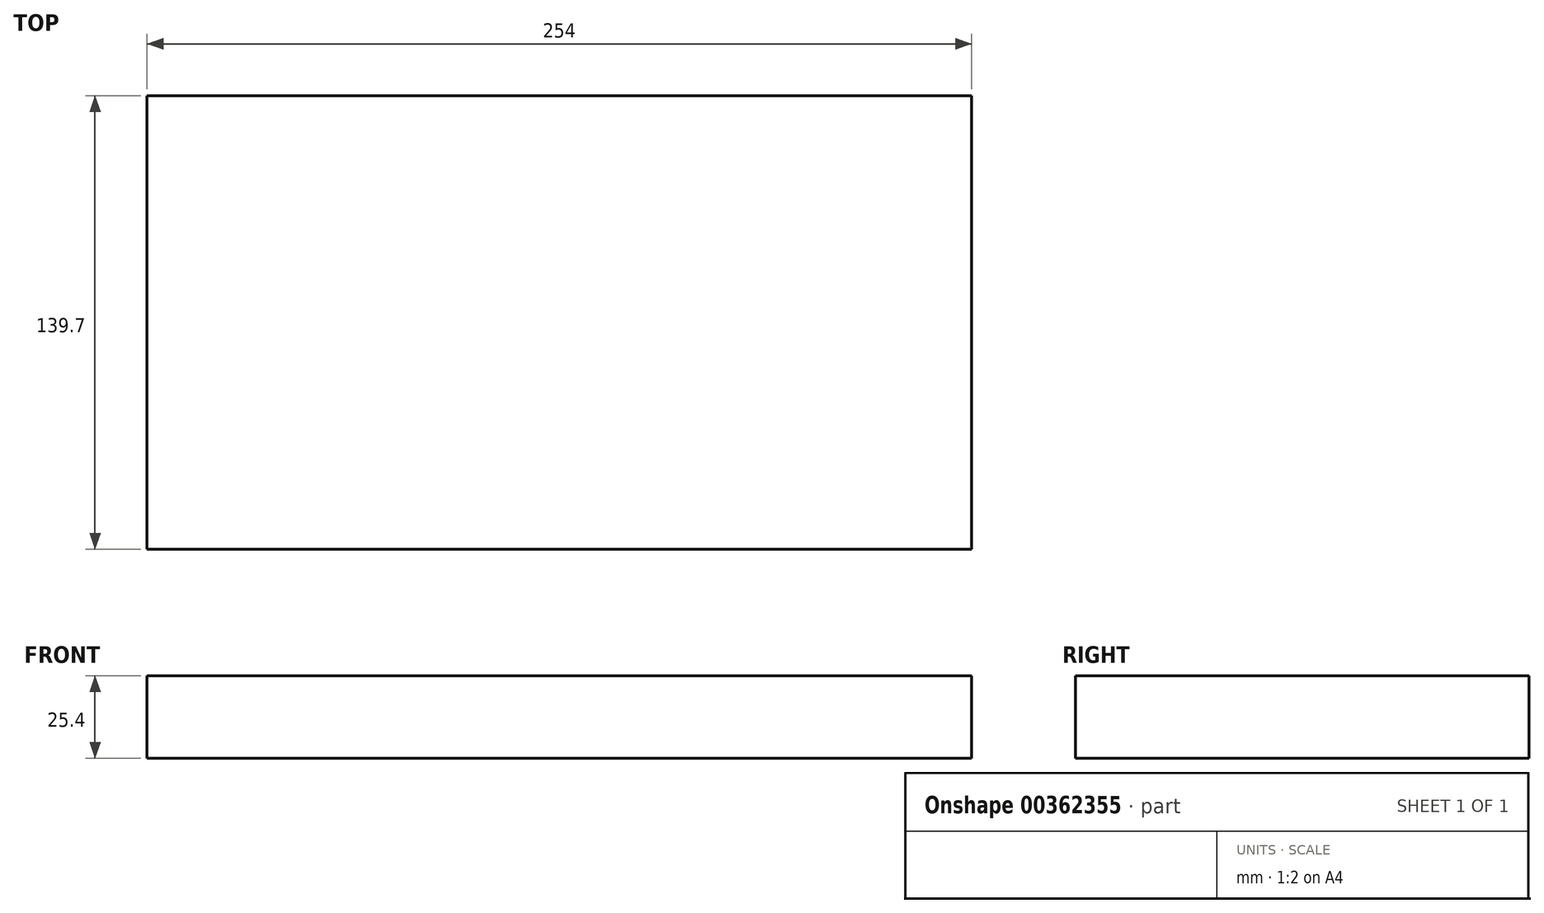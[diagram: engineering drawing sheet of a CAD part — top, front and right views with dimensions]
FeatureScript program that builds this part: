
annotation { "Feature Type Name" : "Feature", "Feature Type Description" : "" }
export const myFeature = defineFeature(function(context is Context, id is Id, definition is map)
    precondition{}
    {
        {
            var Q0;
            Q0=qCreatedBy(makeId("Top.planeOp"),FACE);
            var sketch = newSketch(context, id + "F0", { "sketchPlane" : qUnion([Q0])});
            skLineSegment(sketch, "E0.bottom", {"start": v(-105.82, 62.43) * mm, "end": v(148.18, 62.43) * mm});
            skLineSegment(sketch, "E0.top", {"start": v(-105.82, -77.27) * mm, "end": v(148.18, -77.27) * mm});
            skLineSegment(sketch, "E0.left", {"start": v(-105.82, 62.43) * mm, "end": v(-105.82, -77.27) * mm});
            skLineSegment(sketch, "E0.right", {"start": v(148.18, 62.43) * mm, "end": v(148.18, -77.27) * mm});
            skSolve(sketch);
        }
        {
            var Q0;
            Q0=makeQuery(id+"F0.imprint","IMPRINT",FACE,{"disambiguationData":[TD([[makeQuery(id+"F0.imprint","IMPRINT",EDGE,{"derivedFrom":sQuery(id+"F0.wireOp",EDGE,"E0.bottom")}),-1.0]])]});
            extrude(context, id + "F1", {"entities" : qUnion([Q0]), "depth" : 25.4 * mm});
        }
    });
